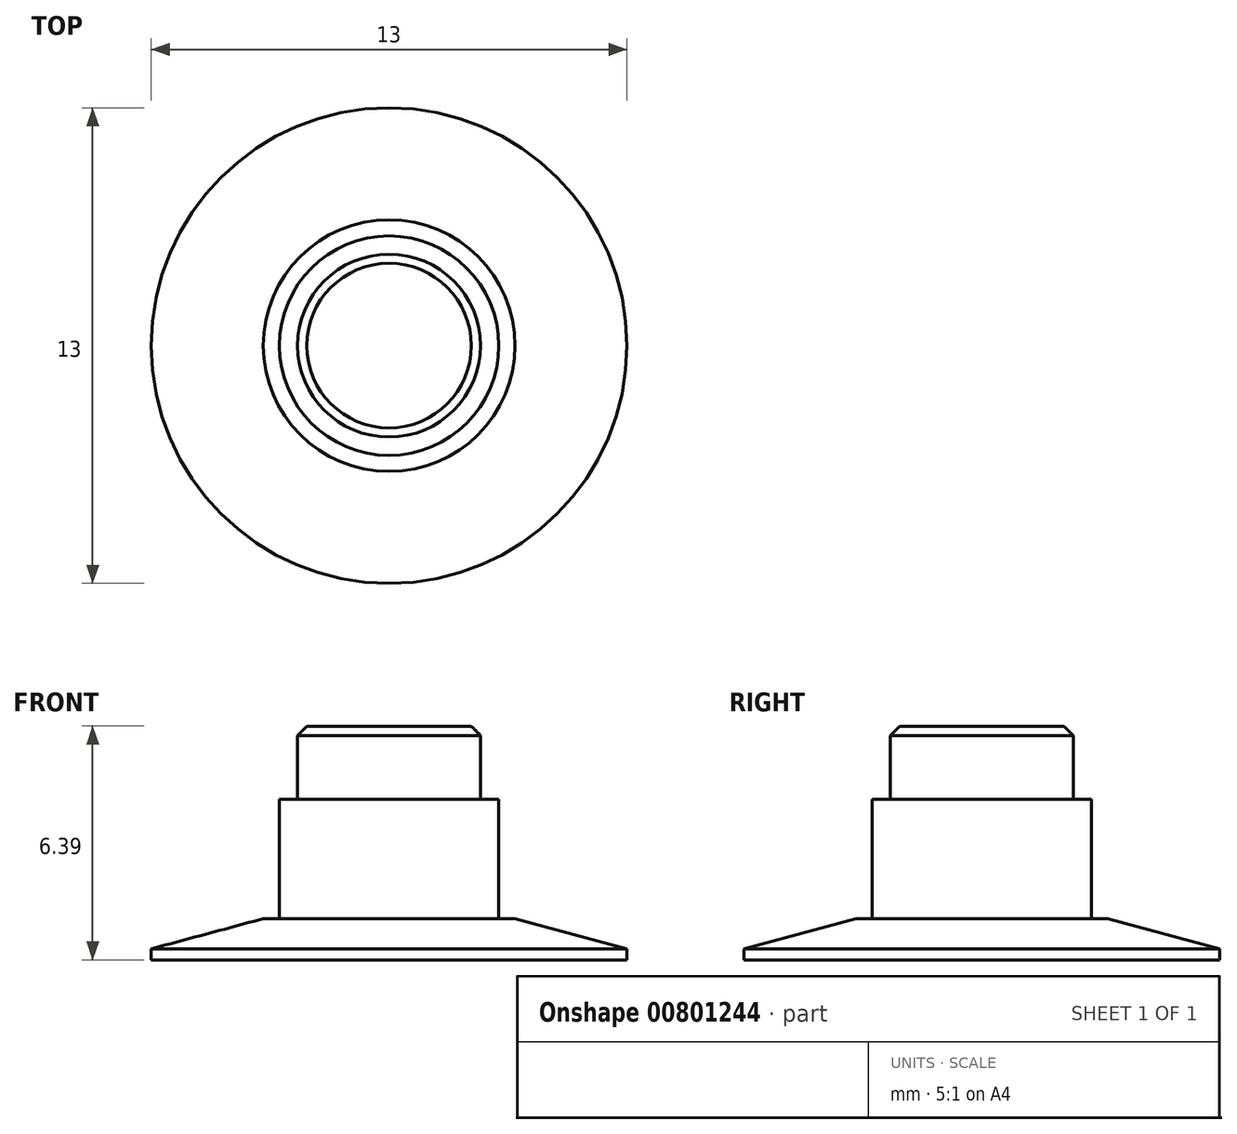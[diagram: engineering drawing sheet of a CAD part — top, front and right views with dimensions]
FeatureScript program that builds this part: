
annotation { "Feature Type Name" : "Feature", "Feature Type Description" : "" }
export const myFeature = defineFeature(function(context is Context, id is Id, definition is map)
    precondition{}
    {
        {
            var Q0;
            Q0=qCreatedBy(makeId("Top.planeOp"),FACE);
            var sketch = newSketch(context, id + "F0", { "sketchPlane" : qUnion([Q0])});
            skCircle(sketch, "E0", {"center": v(0, 0) * mm, "radius": 6.5 * mm});
            skCircle(sketch, "E1", {"center": v(0, 0) * mm, "radius": 3 * mm});
            skCircle(sketch, "E2", {"center": v(0, 0) * mm, "radius": 2.5 * mm});
            skSolve(sketch);
        }
        {
            var Q0;
            Q0=makeQuery(id+"F0.imprint","IMPRINT",FACE,{"disambiguationData":[TD([[makeQuery(id+"F0.imprint","IMPRINT",EDGE,{"derivedFrom":sQuery(id+"F0.wireOp",EDGE,"E2")}),1.0]])]});
            extrude(context, id + "F1", {"entities" : qUnion([Q0]), "depth" : 3.38 * mm, "offsetDistance" : 25 * mm});
        }
        {
            var Q0;
            Q0=makeQuery(id+"F0.imprint","IMPRINT",FACE,{"disambiguationData":[TD([[makeQuery(id+"F0.imprint","IMPRINT",EDGE,{"derivedFrom":sQuery(id+"F0.wireOp",EDGE,"E1")}),1.0]])]});
            extrude(context, id + "F2", {"entities" : qUnion([Q0]), "operationType" : NewBodyOperationType.ADD, "depth" : 1.38 * mm, "offsetDistance" : 25 * mm});
        }
        {
            var Q0;
            Q0=makeQuery(id+"F0.imprint","IMPRINT",FACE,{"disambiguationData":[TD([[makeQuery(id+"F0.imprint","IMPRINT",EDGE,{"derivedFrom":sQuery(id+"F0.wireOp",EDGE,"E0")}),1.0]])]});
            extrude(context, id + "F3", {"entities" : qUnion([Q0]), "operationType" : NewBodyOperationType.ADD, "depth" : .875 * mm, "offsetDistance" : 25 * mm});
        }
        {
            var Q0;
            Q0=makeQuery(id+"F0.imprint","IMPRINT",FACE,{"disambiguationData":[TD([[makeQuery(id+"F0.imprint","IMPRINT",EDGE,{"derivedFrom":sQuery(id+"F0.wireOp",EDGE,"E0")}),1.0]])]});
            var Q1;
            Q1=makeQuery(id+"F0.imprint","IMPRINT",FACE,{"disambiguationData":[TD([[makeQuery(id+"F0.imprint","IMPRINT",EDGE,{"derivedFrom":sQuery(id+"F0.wireOp",EDGE,"E2")}),1.0]])]});
            var Q2;
            Q2=makeQuery(id+"F0.imprint","IMPRINT",FACE,{"disambiguationData":[TD([[makeQuery(id+"F0.imprint","IMPRINT",EDGE,{"derivedFrom":sQuery(id+"F0.wireOp",EDGE,"E1")}),1.0]])]});
            extrude(context, id + "F4", {"entities" : qUnion([Q0, Q1, Q2]), "operationType" : NewBodyOperationType.ADD, "oppositeDirection" : true, "depth" : .25 * mm, "offsetDistance" : 25 * mm});
        }
        {
            var Q0;
            Q0=qCreatedBy(makeId("Right.planeOp"),FACE);
            var sketch = newSketch(context, id + "F5", { "sketchPlane" : qUnion([Q0])});
            skLineSegment(sketch, "E3", {"start": v(-6.7, 0) * mm, "end": v(-3.12, 0.96) * mm});
            skLineSegment(sketch, "E4", {"start": v(-3.12, 0.96) * mm, "end": v(-6.7, 0.96) * mm});
            skLineSegment(sketch, "E5", {"start": v(-6.7, 0.96) * mm, "end": v(-6.7, 0) * mm});
            skLineSegment(sketch, "E6", {"start": v(0, -2.7) * mm, "end": v(0, 4.57) * mm, "construction": true});
            skSolve(sketch);
        }
        {
            var Q0;
            Q0=makeQuery(id+"F5.imprint","IMPRINT",FACE,{"disambiguationData":[TD([[makeQuery(id+"F5.imprint","IMPRINT",EDGE,{"derivedFrom":sQuery(id+"F5.wireOp",EDGE,"E3")}),1.0]])]});
            var Q1;
            Q1=sQuery(id+"F5.wireOp",EDGE,"E6");
            revolve(context, id + "F6", {"operationType" : NewBodyOperationType.REMOVE, "surfaceOperationType" : NewSurfaceOperationType.NEW, "entities" : qUnion([Q0]), "axis" : qUnion([Q1]), "revolveType" : RevolveType.FULL, "oppositeDirection" : true});
        }
        {
            var Q0;
            Q0=makeQuery(id+"F2.opExtrude","CAP_FACE",FACE,{"disambiguationData":[OSD([sQuery(id+"F0.wireOp",EDGE,"E1"),sQuery(id+"F0.wireOp",EDGE,"E2")])],"isStart":false});
            extrude(context, id + "F7", {"entities" : qUnion([Q0]), "operationType" : NewBodyOperationType.ADD, "depth" : 2.76 * mm, "offsetDistance" : 25 * mm});
        }
        {
            var Q0;
            Q0=makeQuery(id+"F1.opExtrude","CAP_FACE",FACE,{"disambiguationData":[OSD([sQuery(id+"F0.wireOp",EDGE,"E2")])],"isStart":false});
            extrude(context, id + "F8", {"entities" : qUnion([Q0]), "operationType" : NewBodyOperationType.ADD, "depth" : 2.76 * mm, "offsetDistance" : 25 * mm});
        }
        {
            var Q0;
            Q0=makeQuery(id+"F8.opExtrude","CAP_EDGE",EDGE,{"disambiguationData":[OSD([sQuery(id+"F0.wireOp",EDGE,"E2")])],"isStart":false});
            chamfer(context, id + "F9", {"entities" : qUnion([Q0]), "width" : .25 * mm, "tangentPropagation" : true});
        }
    });
